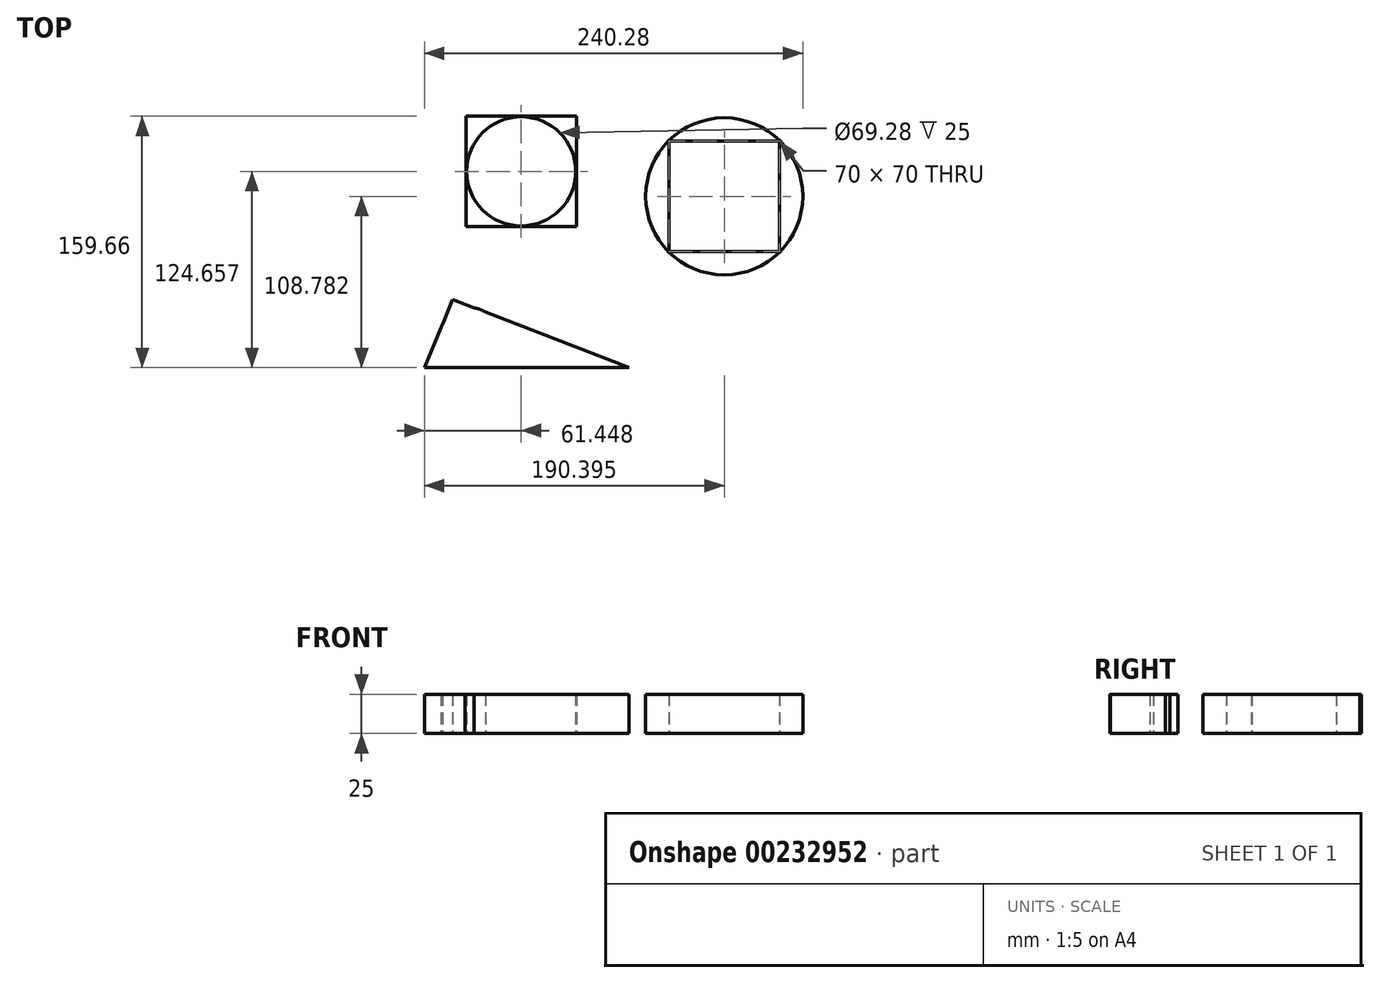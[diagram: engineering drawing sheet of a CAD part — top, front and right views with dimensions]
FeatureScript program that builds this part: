
annotation { "Feature Type Name" : "Feature", "Feature Type Description" : "" }
export const myFeature = defineFeature(function(context is Context, id is Id, definition is map)
    precondition{}
    {
        {
            var Q0;
            Q0=qCreatedBy(makeId("Top.planeOp"),FACE);
            var sketch = newSketch(context, id + "F0", { "sketchPlane" : qUnion([Q0])});
            skLineSegment(sketch, "E0", {"start": v(-66.22, 66.7) * mm, "end": v(-66.22, -3.3) * mm});
            skLineSegment(sketch, "E1", {"start": v(-66.22, -3.3) * mm, "end": v(3.78, -3.3) * mm});
            skLineSegment(sketch, "E2", {"start": v(3.78, -3.3) * mm, "end": v(3.78, 66.7) * mm});
            skLineSegment(sketch, "E3", {"start": v(-66.22, 66.7) * mm, "end": v(3.78, 66.7) * mm});
            skLineSegment(sketch, "E4", {"start": v(-50.18, 24.31) * mm, "end": v(-50.18, 25.86) * mm});
            skCircle(sketch, "E5", {"center": v(-31.22, 31.7) * mm, "radius": 34.64 * mm});
            skLineSegment(sketch, "E6", {"start": v(62.72, 50.83) * mm, "end": v(132.72, 50.83) * mm});
            skLineSegment(sketch, "E7", {"start": v(62.72, 50.83) * mm, "end": v(62.72, -19.17) * mm});
            skLineSegment(sketch, "E8", {"start": v(62.72, -19.17) * mm, "end": v(132.72, -19.17) * mm});
            skLineSegment(sketch, "E9", {"start": v(132.72, 50.83) * mm, "end": v(132.72, -19.17) * mm});
            skCircle(sketch, "E10", {"center": v(97.72, 15.83) * mm, "radius": 49.88 * mm});
            skLineSegment(sketch, "E11", {"start": v(-92.67, -92.74) * mm, "end": v(37.33, -92.74) * mm});
            skLineSegment(sketch, "E12", {"start": v(37.33, -92.74) * mm, "end": v(-74.7, -49.74) * mm});
            skLineSegment(sketch, "E13", {"start": v(-74.7, -49.74) * mm, "end": v(-92.67, -92.74) * mm});
            skLineSegment(sketch, "E14", {"start": v(-59.41, -92.74) * mm, "end": v(-92.67, -92.74) * mm});
            skPoint(sketch, "E15.first.point", {"position": v(-79.4, -60.98) * mm});
            skPoint(sketch, "E15.second.point", {"position": v(-51.15, -58.78) * mm});
            skPoint(sketch, "E15.third.point", {"position": v(-41.12, -92.74) * mm});
            skPoint(sketch, "E16.first.point", {"position": v(-83.69, -71.24) * mm});
            skPoint(sketch, "E16.second.point", {"position": v(-46.67, -76.67) * mm});
            skPoint(sketch, "E16.third.point", {"position": v(-60.98, -55) * mm});
            skCircle(sketch, "E17", {"center": v(-64.11, -73.85) * mm, "radius": 19.1 * mm});
            skPoint(sketch, "E17.first.point", {"position": v(-66.9, -92.74) * mm});
            skPoint(sketch, "E17.third.point", {"position": v(-76.04, -58.93) * mm});
            skSolve(sketch);
        }
        {
            var Q0;
            Q0 = qSketchRegion(id + "F0", true);
            extrude(context, id + "F1", {"entities" : qUnion([Q0]), "depth" : 25 * mm});
        }
    });
